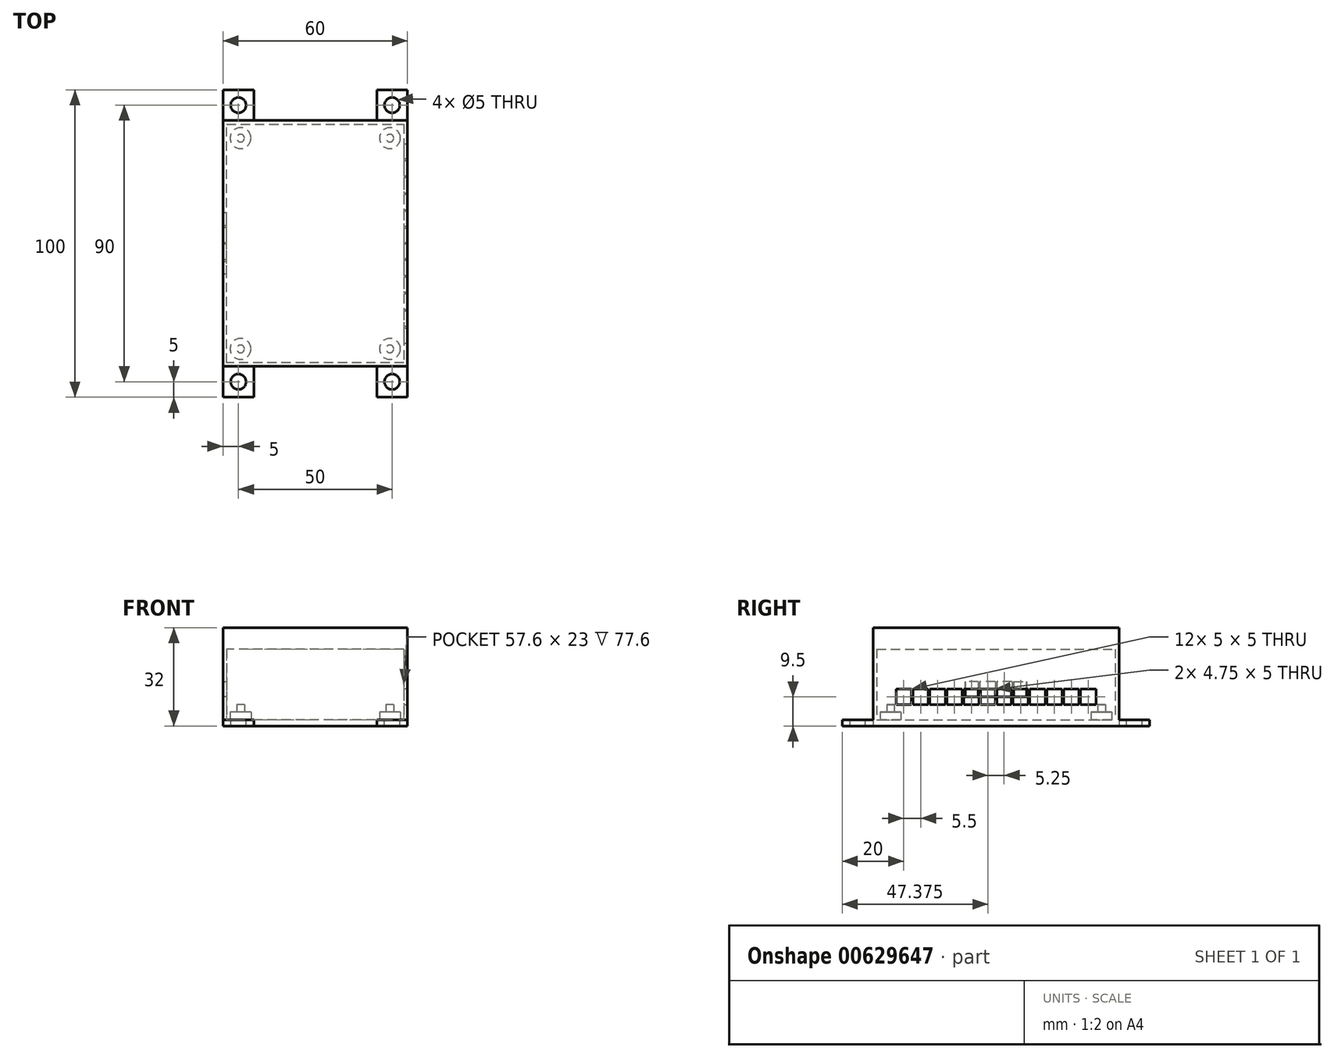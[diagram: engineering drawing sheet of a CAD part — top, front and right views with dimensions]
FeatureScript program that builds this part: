
annotation { "Feature Type Name" : "Feature", "Feature Type Description" : "" }
export const myFeature = defineFeature(function(context is Context, id is Id, definition is map)
    precondition{}
    {
        {
            var Q0;
            Q0=qCreatedBy(makeId("Top.planeOp"),FACE);
            var sketch = newSketch(context, id + "F0", { "sketchPlane" : qUnion([Q0])});
            skLineSegment(sketch, "E0", {"start": v(0, 0) * mm, "end": v(10, 0) * mm});
            skLineSegment(sketch, "E1", {"start": v(10, 0) * mm, "end": v(10, 10) * mm});
            skLineSegment(sketch, "E2", {"start": v(10, 10) * mm, "end": v(50, 10) * mm});
            skLineSegment(sketch, "E3", {"start": v(50, 10) * mm, "end": v(50, 0) * mm});
            skLineSegment(sketch, "E4", {"start": v(50, 0) * mm, "end": v(60, 0) * mm});
            skLineSegment(sketch, "E5", {"start": v(60, 0) * mm, "end": v(60, 100) * mm});
            skLineSegment(sketch, "E6", {"start": v(60, 100) * mm, "end": v(50, 100) * mm});
            skLineSegment(sketch, "E7", {"start": v(50, 100) * mm, "end": v(50, 90) * mm});
            skLineSegment(sketch, "E8", {"start": v(50, 90) * mm, "end": v(10, 90) * mm});
            skLineSegment(sketch, "E9", {"start": v(10, 90) * mm, "end": v(10, 100) * mm});
            skLineSegment(sketch, "E10", {"start": v(10, 100) * mm, "end": v(0, 100) * mm});
            skLineSegment(sketch, "E11", {"start": v(0, 100) * mm, "end": v(0, 0) * mm});
            skSolve(sketch);
        }
        {
            var Q0;
            Q0=makeQuery(id+"F0.imprint","IMPRINT",FACE,{"disambiguationData":[TD([[makeQuery(id+"F0.imprint","IMPRINT",EDGE,{"derivedFrom":sQuery(id+"F0.wireOp",EDGE,"E0")}),1.0]])]});
            extrude(context, id + "F1", {"entities" : qUnion([Q0]), "depth" : 2 * mm, "offsetDistance" : 25 * mm});
        }
        {
            var Q0;
            Q0=makeQuery(id+"F1.opExtrude","CAP_FACE",FACE,{"disambiguationData":[OSD([sQuery(id+"F0.wireOp",EDGE,"E0"),sQuery(id+"F0.wireOp",EDGE,"E1"),sQuery(id+"F0.wireOp",EDGE,"E2"),sQuery(id+"F0.wireOp",EDGE,"E3"),sQuery(id+"F0.wireOp",EDGE,"E4"),sQuery(id+"F0.wireOp",EDGE,"E5"),sQuery(id+"F0.wireOp",EDGE,"E6"),sQuery(id+"F0.wireOp",EDGE,"E7"),sQuery(id+"F0.wireOp",EDGE,"E8"),sQuery(id+"F0.wireOp",EDGE,"E9"),sQuery(id+"F0.wireOp",EDGE,"E10"),sQuery(id+"F0.wireOp",EDGE,"E11")])],"isStart":false});
            var sketch = newSketch(context, id + "F2", { "sketchPlane" : qUnion([Q0])});
            skLineSegment(sketch, "E12", {"start": v(60, 10) * mm, "end": v(0, 10) * mm});
            skLineSegment(sketch, "E13", {"start": v(0, 10) * mm, "end": v(0, 90) * mm});
            skLineSegment(sketch, "E14", {"start": v(0, 90) * mm, "end": v(60, 90) * mm});
            skLineSegment(sketch, "E15", {"start": v(60, 90) * mm, "end": v(60, 10) * mm});
            skLineSegment(sketch, "E16.0", {"start": v(1.2, 11.2) * mm, "end": v(1.2, 88.8) * mm});
            skLineSegment(sketch, "E16.1", {"start": v(58.8, 11.2) * mm, "end": v(1.2, 11.2) * mm});
            skLineSegment(sketch, "E16.2", {"start": v(58.8, 88.8) * mm, "end": v(58.8, 11.2) * mm});
            skLineSegment(sketch, "E16.3", {"start": v(1.2, 88.8) * mm, "end": v(58.8, 88.8) * mm});
            skSolve(sketch);
        }
        {
            var Q0;
            Q0 = qSketchRegion(id + "F2", true);
            extrude(context, id + "F3", {"entities" : qUnion([Q0]), "operationType" : NewBodyOperationType.ADD, "depth" : 28 * mm, "offsetDistance" : 25 * mm});
        }
        {
            var Q0;
            {var subQ0=sQuery(id+"F0.wireOp",EDGE,"E2");var subQ1=sQuery(id+"F0.wireOp",EDGE,"E11");var subQ2=sQuery(id+"F0.wireOp",EDGE,"E1");var subQ3=sQuery(id+"F0.wireOp",EDGE,"E0");Q0=makeQuery(id+"F3.boolean.opBoolean","SPLIT",FACE,{"disambiguationData":[TD([makeQuery(id+"F1.opExtrude","SWEPT_FACE",FACE,{"disambiguationData":[OSD([subQ3])]})])],"derivedFrom":makeQuery(id+"F1.opExtrude","CAP_FACE",FACE,{"disambiguationData":[OSD([subQ3,subQ2,subQ0,sQuery(id+"F0.wireOp",EDGE,"E3"),sQuery(id+"F0.wireOp",EDGE,"E4"),sQuery(id+"F0.wireOp",EDGE,"E5"),sQuery(id+"F0.wireOp",EDGE,"E6"),sQuery(id+"F0.wireOp",EDGE,"E7"),sQuery(id+"F0.wireOp",EDGE,"E8"),sQuery(id+"F0.wireOp",EDGE,"E9"),sQuery(id+"F0.wireOp",EDGE,"E10"),subQ1])],"isStart":false})});}
            var sketch = newSketch(context, id + "F4", { "sketchPlane" : qUnion([Q0])});
            skCircle(sketch, "E17", {"center": v(5, 5) * mm, "radius": 2.5 * mm});
            skPoint(sketch, "E17.centerSnap0", {"position": v(5, 0) * mm});
            skPoint(sketch, "E17.centerSnap1", {"position": v(0, 5) * mm});
            skSolve(sketch);
        }
        {
            var Q0;
            {var subQ0=sQuery(id+"F0.wireOp",EDGE,"E5");var subQ1=sQuery(id+"F0.wireOp",EDGE,"E4");var subQ2=sQuery(id+"F0.wireOp",EDGE,"E3");var subQ3=sQuery(id+"F0.wireOp",EDGE,"E2");Q0=makeQuery(id+"F3.boolean.opBoolean","SPLIT",FACE,{"disambiguationData":[TD([makeQuery(id+"F1.opExtrude","SWEPT_FACE",FACE,{"disambiguationData":[OSD([subQ2])]})])],"derivedFrom":makeQuery(id+"F1.opExtrude","CAP_FACE",FACE,{"disambiguationData":[OSD([sQuery(id+"F0.wireOp",EDGE,"E0"),sQuery(id+"F0.wireOp",EDGE,"E1"),subQ3,subQ2,subQ1,subQ0,sQuery(id+"F0.wireOp",EDGE,"E6"),sQuery(id+"F0.wireOp",EDGE,"E7"),sQuery(id+"F0.wireOp",EDGE,"E8"),sQuery(id+"F0.wireOp",EDGE,"E9"),sQuery(id+"F0.wireOp",EDGE,"E10"),sQuery(id+"F0.wireOp",EDGE,"E11")])],"isStart":false})});}
            var sketch = newSketch(context, id + "F5", { "sketchPlane" : qUnion([Q0])});
            skCircle(sketch, "E18", {"center": v(55, 5) * mm, "radius": 2.5 * mm});
            skPoint(sketch, "E18.centerSnap0", {"position": v(60, 5) * mm});
            skPoint(sketch, "E18.centerSnap1", {"position": v(55, 0) * mm});
            skSolve(sketch);
        }
        {
            var Q0;
            {var subQ0=sQuery(id+"F0.wireOp",EDGE,"E8");var subQ1=sQuery(id+"F0.wireOp",EDGE,"E7");var subQ2=sQuery(id+"F0.wireOp",EDGE,"E6");var subQ3=sQuery(id+"F0.wireOp",EDGE,"E5");Q0=makeQuery(id+"F3.boolean.opBoolean","SPLIT",FACE,{"disambiguationData":[TD([makeQuery(id+"F1.opExtrude","SWEPT_FACE",FACE,{"disambiguationData":[OSD([subQ2])]})])],"derivedFrom":makeQuery(id+"F1.opExtrude","CAP_FACE",FACE,{"disambiguationData":[OSD([sQuery(id+"F0.wireOp",EDGE,"E0"),sQuery(id+"F0.wireOp",EDGE,"E1"),sQuery(id+"F0.wireOp",EDGE,"E2"),sQuery(id+"F0.wireOp",EDGE,"E3"),sQuery(id+"F0.wireOp",EDGE,"E4"),subQ3,subQ2,subQ1,subQ0,sQuery(id+"F0.wireOp",EDGE,"E9"),sQuery(id+"F0.wireOp",EDGE,"E10"),sQuery(id+"F0.wireOp",EDGE,"E11")])],"isStart":false})});}
            var sketch = newSketch(context, id + "F6", { "sketchPlane" : qUnion([Q0])});
            skCircle(sketch, "E19", {"center": v(55, 95) * mm, "radius": 2.5 * mm});
            skPoint(sketch, "E19.centerSnap0", {"position": v(60, 95) * mm});
            skPoint(sketch, "E19.centerSnap1", {"position": v(55, 100) * mm});
            skSolve(sketch);
        }
        {
            var Q0;
            {var subQ0=sQuery(id+"F0.wireOp",EDGE,"E11");var subQ1=sQuery(id+"F0.wireOp",EDGE,"E10");var subQ2=sQuery(id+"F0.wireOp",EDGE,"E9");var subQ3=sQuery(id+"F0.wireOp",EDGE,"E8");Q0=makeQuery(id+"F3.boolean.opBoolean","SPLIT",FACE,{"disambiguationData":[TD([makeQuery(id+"F1.opExtrude","SWEPT_FACE",FACE,{"disambiguationData":[OSD([subQ2])]})])],"derivedFrom":makeQuery(id+"F1.opExtrude","CAP_FACE",FACE,{"disambiguationData":[OSD([sQuery(id+"F0.wireOp",EDGE,"E0"),sQuery(id+"F0.wireOp",EDGE,"E1"),sQuery(id+"F0.wireOp",EDGE,"E2"),sQuery(id+"F0.wireOp",EDGE,"E3"),sQuery(id+"F0.wireOp",EDGE,"E4"),sQuery(id+"F0.wireOp",EDGE,"E5"),sQuery(id+"F0.wireOp",EDGE,"E6"),sQuery(id+"F0.wireOp",EDGE,"E7"),subQ3,subQ2,subQ1,subQ0])],"isStart":false})});}
            var sketch = newSketch(context, id + "F7", { "sketchPlane" : qUnion([Q0])});
            skCircle(sketch, "E20", {"center": v(5, 95) * mm, "radius": 2.5 * mm});
            skPoint(sketch, "E20.centerSnap0", {"position": v(5, 100) * mm});
            skPoint(sketch, "E20.centerSnap1", {"position": v(0, 95) * mm});
            skSolve(sketch);
        }
        {
            var Q0;
            Q0 = qSketchRegion(id + "F7", true);
            var Q1;
            Q1 = qSketchRegion(id + "F6", true);
            var Q2;
            Q2 = qSketchRegion(id + "F5", true);
            var Q3;
            Q3 = qSketchRegion(id + "F4", true);
            extrude(context, id + "F8", {"entities" : qUnion([Q0, Q1, Q2, Q3]), "operationType" : NewBodyOperationType.REMOVE, "endBound" : BoundingType.UP_TO_NEXT, "oppositeDirection" : true, "depth" : 25 * mm, "offsetDistance" : 25 * mm});
        }
        {
            var Q0;
            Q0=makeQuery(id+"F3.boolean.opBoolean","SPLIT",FACE,{"disambiguationData":[TD([makeQuery(id+"F3.opExtrude","SWEPT_FACE",FACE,{"disambiguationData":[OSD([sQuery(id+"F2.wireOp",EDGE,"E16.0")])]})])],"derivedFrom":makeQuery(id+"F1.opExtrude","CAP_FACE",FACE,{"disambiguationData":[OSD([sQuery(id+"F0.wireOp",EDGE,"E0"),sQuery(id+"F0.wireOp",EDGE,"E1"),sQuery(id+"F0.wireOp",EDGE,"E2"),sQuery(id+"F0.wireOp",EDGE,"E3"),sQuery(id+"F0.wireOp",EDGE,"E4"),sQuery(id+"F0.wireOp",EDGE,"E5"),sQuery(id+"F0.wireOp",EDGE,"E6"),sQuery(id+"F0.wireOp",EDGE,"E7"),sQuery(id+"F0.wireOp",EDGE,"E8"),sQuery(id+"F0.wireOp",EDGE,"E9"),sQuery(id+"F0.wireOp",EDGE,"E10"),sQuery(id+"F0.wireOp",EDGE,"E11")])],"isStart":false})});
            var sketch = newSketch(context, id + "F9", { "sketchPlane" : qUnion([Q0])});
            skCircle(sketch, "E21", {"center": v(5.7, 15.7) * mm, "radius": 3.4 * mm});
            skCircle(sketch, "E22", {"center": v(5.7, 84.29) * mm, "radius": 3.4 * mm});
            skCircle(sketch, "E23", {"center": v(54.3, 15.7) * mm, "radius": 3.4 * mm});
            skCircle(sketch, "E24", {"center": v(54.29, 84.29) * mm, "radius": 3.4 * mm});
            skSolve(sketch);
        }
        {
            var Q0;
            Q0=makeQuery(id+"F9.imprint","IMPRINT",FACE,{"disambiguationData":[TD([[makeQuery(id+"F9.imprint","IMPRINT",EDGE,{"derivedFrom":sQuery(id+"F9.wireOp",EDGE,"E21")}),1.0]])]});
            var Q1;
            Q1=makeQuery(id+"F9.imprint","IMPRINT",FACE,{"disambiguationData":[TD([[makeQuery(id+"F9.imprint","IMPRINT",EDGE,{"derivedFrom":sQuery(id+"F9.wireOp",EDGE,"E22")}),1.0]])]});
            var Q2;
            Q2=makeQuery(id+"F9.imprint","IMPRINT",FACE,{"disambiguationData":[TD([[makeQuery(id+"F9.imprint","IMPRINT",EDGE,{"derivedFrom":sQuery(id+"F9.wireOp",EDGE,"E23")}),1.0]])]});
            var Q3;
            Q3=makeQuery(id+"F9.imprint","IMPRINT",FACE,{"disambiguationData":[TD([[makeQuery(id+"F9.imprint","IMPRINT",EDGE,{"derivedFrom":sQuery(id+"F9.wireOp",EDGE,"E24")}),1.0]])]});
            extrude(context, id + "F10", {"entities" : qUnion([Q0, Q1, Q2, Q3]), "operationType" : NewBodyOperationType.ADD, "depth" : 2.5 * mm, "offsetDistance" : 25 * mm});
        }
        {
            var Q0;
            Q0=makeQuery(id+"F10.opExtrude","CAP_FACE",FACE,{"disambiguationData":[OSD([sQuery(id+"F9.wireOp",EDGE,"E21")])],"isStart":false});
            var sketch = newSketch(context, id + "F11", { "sketchPlane" : qUnion([Q0])});
            skCircle(sketch, "E25", {"center": v(5.7, 15.7) * mm, "radius": 1.25 * mm});
            skSolve(sketch);
        }
        {
            var Q0;
            Q0=makeQuery(id+"F10.opExtrude","CAP_FACE",FACE,{"disambiguationData":[OSD([sQuery(id+"F9.wireOp",EDGE,"E23")])],"isStart":false});
            var sketch = newSketch(context, id + "F12", { "sketchPlane" : qUnion([Q0])});
            skCircle(sketch, "E26", {"center": v(54.3, 15.7) * mm, "radius": 1.25 * mm});
            skSolve(sketch);
        }
        {
            var Q0;
            Q0=makeQuery(id+"F10.opExtrude","CAP_FACE",FACE,{"disambiguationData":[OSD([sQuery(id+"F9.wireOp",EDGE,"E24")])],"isStart":false});
            var sketch = newSketch(context, id + "F13", { "sketchPlane" : qUnion([Q0])});
            skCircle(sketch, "E27", {"center": v(54.29, 84.29) * mm, "radius": 1.25 * mm});
            skSolve(sketch);
        }
        {
            var Q0;
            Q0=makeQuery(id+"F10.opExtrude","CAP_FACE",FACE,{"disambiguationData":[OSD([sQuery(id+"F9.wireOp",EDGE,"E22")])],"isStart":false});
            var sketch = newSketch(context, id + "F14", { "sketchPlane" : qUnion([Q0])});
            skCircle(sketch, "E28", {"center": v(5.7, 84.29) * mm, "radius": 1.25 * mm});
            skSolve(sketch);
        }
        {
            var Q0;
            Q0 = qSketchRegion(id + "F14", true);
            var Q1;
            Q1 = qSketchRegion(id + "F13", true);
            var Q2;
            Q2 = qSketchRegion(id + "F11", true);
            var Q3;
            Q3 = qSketchRegion(id + "F12", true);
            extrude(context, id + "F15", {"entities" : qUnion([Q0, Q1, Q2, Q3]), "operationType" : NewBodyOperationType.ADD, "depth" : 2.5 * mm, "offsetDistance" : 25 * mm});
        }
        {
            var Q0;
            Q0=makeQuery(id+"F3.boolean.opBoolean","MERGE",FACE,{"derivedFrom":[makeQuery(id+"F1.opExtrude","SWEPT_FACE",FACE,{"disambiguationData":[OSD([sQuery(id+"F0.wireOp",EDGE,"E5")])]}),makeQuery(id+"F3.opExtrude","SWEPT_FACE",FACE,{"disambiguationData":[OSD([sQuery(id+"F2.wireOp",EDGE,"E15")])]})]});
            var sketch = newSketch(context, id + "F16", { "sketchPlane" : qUnion([Q0])});
            skLineSegment(sketch, "E29.bottom", {"start": v(17.5, 12) * mm, "end": v(82.5, 12) * mm});
            skLineSegment(sketch, "E29.top", {"start": v(17.5, 7) * mm, "end": v(82.5, 7) * mm});
            skLineSegment(sketch, "E29.left", {"start": v(17.5, 12) * mm, "end": v(17.5, 7) * mm});
            skLineSegment(sketch, "E29.right", {"start": v(82.5, 12) * mm, "end": v(82.5, 7) * mm});
            skSolve(sketch);
        }
        {
            var Q0;
            Q0=makeQuery(id+"F16.imprint","IMPRINT",FACE,{"disambiguationData":[TD([[makeQuery(id+"F16.imprint","IMPRINT",EDGE,{"derivedFrom":sQuery(id+"F16.wireOp",EDGE,"E29.bottom")}),-1.0]])]});
            extrude(context, id + "F17", {"entities" : qUnion([Q0]), "operationType" : NewBodyOperationType.REMOVE, "endBound" : BoundingType.UP_TO_NEXT, "oppositeDirection" : true, "depth" : 25 * mm, "offsetDistance" : 25 * mm});
        }
        {
            var Q0;
            Q0=makeQuery(id+"F17.boolean.opBoolean","COPY",FACE,{"derivedFrom":makeQuery(id+"F17.opExtrude","SWEPT_FACE",FACE,{"disambiguationData":[OSD([sQuery(id+"F16.wireOp",EDGE,"E29.top")])]})});
            var sketch = newSketch(context, id + "F18", { "sketchPlane" : qUnion([Q0])});
            skLineSegment(sketch, "E30.0", {"start": v(58.8, 49.75) * mm, "end": v(60, 49.75) * mm});
            skLineSegment(sketch, "E31.0", {"start": v(58.8, 50.25) * mm, "end": v(60, 50.25) * mm});
            skLineSegment(sketch, "E32", {"start": v(58.8, 49.75) * mm, "end": v(58.8, 50.25) * mm});
            skLineSegment(sketch, "E33", {"start": v(60, 49.75) * mm, "end": v(60, 50.25) * mm});
            skLineSegment(sketch, "E34.bottom", {"start": v(58.8, 44.5) * mm, "end": v(60, 44.5) * mm});
            skLineSegment(sketch, "E34.top", {"start": v(58.8, 45) * mm, "end": v(60, 45) * mm});
            skLineSegment(sketch, "E34.left", {"start": v(58.8, 44.5) * mm, "end": v(58.8, 45) * mm});
            skLineSegment(sketch, "E34.right", {"start": v(60, 44.5) * mm, "end": v(60, 45) * mm});
            skLineSegment(sketch, "E35.bottom", {"start": v(58.8, 39.5) * mm, "end": v(60, 39.5) * mm});
            skLineSegment(sketch, "E35.top", {"start": v(58.8, 39) * mm, "end": v(60, 39) * mm});
            skLineSegment(sketch, "E35.left", {"start": v(58.8, 39.5) * mm, "end": v(58.8, 39) * mm});
            skLineSegment(sketch, "E35.right", {"start": v(60, 39.5) * mm, "end": v(60, 39) * mm});
            skLineSegment(sketch, "E36.bottom", {"start": v(58.8, 34) * mm, "end": v(60, 34) * mm});
            skLineSegment(sketch, "E36.top", {"start": v(58.8, 33.5) * mm, "end": v(60, 33.5) * mm});
            skLineSegment(sketch, "E36.left", {"start": v(58.8, 34) * mm, "end": v(58.8, 33.5) * mm});
            skLineSegment(sketch, "E36.right", {"start": v(60, 34) * mm, "end": v(60, 33.5) * mm});
            skLineSegment(sketch, "E37.bottom", {"start": v(58.8, 28.5) * mm, "end": v(60, 28.5) * mm});
            skLineSegment(sketch, "E37.top", {"start": v(58.8, 28) * mm, "end": v(60, 28) * mm});
            skLineSegment(sketch, "E37.left", {"start": v(58.8, 28.5) * mm, "end": v(58.8, 28) * mm});
            skLineSegment(sketch, "E37.right", {"start": v(60, 28.5) * mm, "end": v(60, 28) * mm});
            skLineSegment(sketch, "E38.bottom", {"start": v(58.8, 23) * mm, "end": v(60, 23) * mm});
            skLineSegment(sketch, "E38.top", {"start": v(58.8, 22.5) * mm, "end": v(60, 22.5) * mm});
            skLineSegment(sketch, "E38.left", {"start": v(58.8, 23) * mm, "end": v(58.8, 22.5) * mm});
            skLineSegment(sketch, "E38.right", {"start": v(60, 23) * mm, "end": v(60, 22.5) * mm});
            skLineSegment(sketch, "E39.bottom", {"start": v(58.8, 60.5) * mm, "end": v(60, 60.5) * mm});
            skLineSegment(sketch, "E39.top", {"start": v(58.8, 61) * mm, "end": v(60, 61) * mm});
            skLineSegment(sketch, "E39.left", {"start": v(58.8, 60.5) * mm, "end": v(58.8, 61) * mm});
            skLineSegment(sketch, "E39.right", {"start": v(60, 60.5) * mm, "end": v(60, 61) * mm});
            skLineSegment(sketch, "E40.bottom", {"start": v(58.8, 55) * mm, "end": v(60, 55) * mm});
            skLineSegment(sketch, "E40.top", {"start": v(58.8, 55.5) * mm, "end": v(60, 55.5) * mm});
            skLineSegment(sketch, "E40.left", {"start": v(58.8, 55) * mm, "end": v(58.8, 55.5) * mm});
            skLineSegment(sketch, "E40.right", {"start": v(60, 55) * mm, "end": v(60, 55.5) * mm});
            skLineSegment(sketch, "E41.bottom", {"start": v(58.8, 66) * mm, "end": v(60, 66) * mm});
            skLineSegment(sketch, "E41.top", {"start": v(58.8, 66.5) * mm, "end": v(60, 66.5) * mm});
            skLineSegment(sketch, "E41.left", {"start": v(58.8, 66) * mm, "end": v(58.8, 66.5) * mm});
            skLineSegment(sketch, "E41.right", {"start": v(60, 66) * mm, "end": v(60, 66.5) * mm});
            skLineSegment(sketch, "E42.bottom", {"start": v(58.8, 71.5) * mm, "end": v(60, 71.5) * mm});
            skLineSegment(sketch, "E42.top", {"start": v(58.8, 72) * mm, "end": v(60, 72) * mm});
            skLineSegment(sketch, "E42.left", {"start": v(58.8, 71.5) * mm, "end": v(58.8, 72) * mm});
            skLineSegment(sketch, "E42.right", {"start": v(60, 71.5) * mm, "end": v(60, 72) * mm});
            skLineSegment(sketch, "E43.bottom", {"start": v(58.8, 77) * mm, "end": v(60, 77) * mm});
            skLineSegment(sketch, "E43.top", {"start": v(58.8, 77.5) * mm, "end": v(60, 77.5) * mm});
            skLineSegment(sketch, "E43.left", {"start": v(58.8, 77) * mm, "end": v(58.8, 77.5) * mm});
            skLineSegment(sketch, "E43.right", {"start": v(60, 77) * mm, "end": v(60, 77.5) * mm});
            skSolve(sketch);
        }
        {
            var Q0;
            Q0 = qSketchRegion(id + "F18", true);
            extrude(context, id + "F19", {"entities" : qUnion([Q0]), "operationType" : NewBodyOperationType.ADD, "endBound" : BoundingType.UP_TO_NEXT, "depth" : 25 * mm, "offsetDistance" : 25 * mm});
        }
        {
            var Q0;
            Q0=makeQuery(id+"F3.boolean.opBoolean","MERGE",FACE,{"derivedFrom":[makeQuery(id+"F1.opExtrude","SWEPT_FACE",FACE,{"disambiguationData":[OSD([sQuery(id+"F0.wireOp",EDGE,"E11")])]}),makeQuery(id+"F3.opExtrude","SWEPT_FACE",FACE,{"disambiguationData":[OSD([sQuery(id+"F2.wireOp",EDGE,"E13")])]})]});
            var sketch = newSketch(context, id + "F20", { "sketchPlane" : qUnion([Q0])});
            skLineSegment(sketch, "E44.bottom", {"start": v(-60, 14.5) * mm, "end": v(-40, 14.5) * mm});
            skLineSegment(sketch, "E44.top", {"start": v(-60, 9.5) * mm, "end": v(-40, 9.5) * mm});
            skLineSegment(sketch, "E44.left", {"start": v(-60, 14.5) * mm, "end": v(-60, 9.5) * mm});
            skLineSegment(sketch, "E44.right", {"start": v(-40, 14.5) * mm, "end": v(-40, 9.5) * mm});
            skSolve(sketch);
        }
        {
            var Q0;
            Q0 = qSketchRegion(id + "F20", true);
            extrude(context, id + "F21", {"entities" : qUnion([Q0]), "operationType" : NewBodyOperationType.REMOVE, "endBound" : BoundingType.UP_TO_NEXT, "oppositeDirection" : true, "depth" : 25 * mm, "offsetDistance" : 25 * mm});
        }
        {
            var Q0;
            Q0=makeQuery(id+"F3.opExtrude","CAP_FACE",FACE,{"disambiguationData":[OSD([sQuery(id+"F2.wireOp",EDGE,"E12"),sQuery(id+"F2.wireOp",EDGE,"E13"),sQuery(id+"F2.wireOp",EDGE,"E14"),sQuery(id+"F2.wireOp",EDGE,"E15"),sQuery(id+"F2.wireOp",EDGE,"E16.0"),sQuery(id+"F2.wireOp",EDGE,"E16.1"),sQuery(id+"F2.wireOp",EDGE,"E16.2"),sQuery(id+"F2.wireOp",EDGE,"E16.3")])],"isStart":false});
            var sketch = newSketch(context, id + "F22", { "sketchPlane" : qUnion([Q0])});
            skLineSegment(sketch, "E45.bottom", {"start": v(60, 90) * mm, "end": v(0, 90) * mm});
            skLineSegment(sketch, "E45.top", {"start": v(60, 10) * mm, "end": v(0, 10) * mm});
            skLineSegment(sketch, "E45.left", {"start": v(60, 90) * mm, "end": v(60, 10) * mm});
            skLineSegment(sketch, "E45.right", {"start": v(0, 90) * mm, "end": v(0, 10) * mm});
            skSolve(sketch);
        }
        {
            var Q0;
            Q0 = qSketchRegion(id + "F22", true);
            extrude(context, id + "F23", {"entities" : qUnion([Q0]), "depth" : 2 * mm, "offsetDistance" : 25 * mm});
        }
        {
            var Q0;
            Q0=makeQuery(id+"F3.opExtrude","CAP_FACE",FACE,{"disambiguationData":[OSD([sQuery(id+"F2.wireOp",EDGE,"E12"),sQuery(id+"F2.wireOp",EDGE,"E13"),sQuery(id+"F2.wireOp",EDGE,"E14"),sQuery(id+"F2.wireOp",EDGE,"E15"),sQuery(id+"F2.wireOp",EDGE,"E16.0"),sQuery(id+"F2.wireOp",EDGE,"E16.1"),sQuery(id+"F2.wireOp",EDGE,"E16.2"),sQuery(id+"F2.wireOp",EDGE,"E16.3")])],"isStart":false});
            var sketch = newSketch(context, id + "F24", { "sketchPlane" : qUnion([Q0])});
            skLineSegment(sketch, "E46.bottom", {"start": v(58.8, 88.8) * mm, "end": v(1.2, 88.8) * mm});
            skLineSegment(sketch, "E46.top", {"start": v(58.8, 11.2) * mm, "end": v(1.2, 11.2) * mm});
            skLineSegment(sketch, "E46.left", {"start": v(58.8, 88.8) * mm, "end": v(58.8, 11.2) * mm});
            skLineSegment(sketch, "E46.right", {"start": v(1.2, 88.8) * mm, "end": v(1.2, 11.2) * mm});
            skSolve(sketch);
        }
        {
            var Q0;
            Q0=makeQuery(id+"F24.imprint","IMPRINT",FACE,{"disambiguationData":[TD([[makeQuery(id+"F24.imprint","IMPRINT",EDGE,{"derivedFrom":sQuery(id+"F24.wireOp",EDGE,"E46.bottom")}),-1.0]])]});
            extrude(context, id + "F25", {"entities" : qUnion([Q0]), "operationType" : NewBodyOperationType.ADD, "oppositeDirection" : true, "depth" : 5 * mm, "offsetDistance" : 25 * mm});
        }
        {
            var Q0;
            Q0=makeQuery(id+"F21.boolean.opBoolean","COPY",FACE,{"derivedFrom":makeQuery(id+"F21.opExtrude","SWEPT_FACE",FACE,{"disambiguationData":[OSD([sQuery(id+"F20.wireOp",EDGE,"E44.top")])]})});
            var sketch = newSketch(context, id + "F26", { "sketchPlane" : qUnion([Q0])});
            skLineSegment(sketch, "E47.bottom", {"start": v(1.2, 50.25) * mm, "end": v(0, 50.25) * mm});
            skLineSegment(sketch, "E47.top", {"start": v(1.2, 49.75) * mm, "end": v(0, 49.75) * mm});
            skLineSegment(sketch, "E47.left", {"start": v(1.2, 50.25) * mm, "end": v(1.2, 49.75) * mm});
            skLineSegment(sketch, "E47.right", {"start": v(0, 50.25) * mm, "end": v(0, 49.75) * mm});
            skLineSegment(sketch, "E48.bottom", {"start": v(1.2, 44.75) * mm, "end": v(0, 44.75) * mm});
            skLineSegment(sketch, "E48.top", {"start": v(1.2, 44.25) * mm, "end": v(0, 44.25) * mm});
            skLineSegment(sketch, "E48.left", {"start": v(1.2, 44.75) * mm, "end": v(1.2, 44.25) * mm});
            skLineSegment(sketch, "E48.right", {"start": v(0, 44.75) * mm, "end": v(0, 44.25) * mm});
            skLineSegment(sketch, "E49.bottom", {"start": v(1.2, 55.75) * mm, "end": v(0, 55.75) * mm});
            skLineSegment(sketch, "E49.top", {"start": v(1.2, 55.25) * mm, "end": v(0, 55.25) * mm});
            skLineSegment(sketch, "E49.left", {"start": v(1.2, 55.75) * mm, "end": v(1.2, 55.25) * mm});
            skLineSegment(sketch, "E49.right", {"start": v(0, 55.75) * mm, "end": v(0, 55.25) * mm});
            skSolve(sketch);
        }
        {
            var Q0;
            Q0 = qSketchRegion(id + "F26", true);
            extrude(context, id + "F27", {"entities" : qUnion([Q0]), "operationType" : NewBodyOperationType.ADD, "endBound" : BoundingType.UP_TO_NEXT, "depth" : 25 * mm, "offsetDistance" : 25 * mm});
        }
    });
